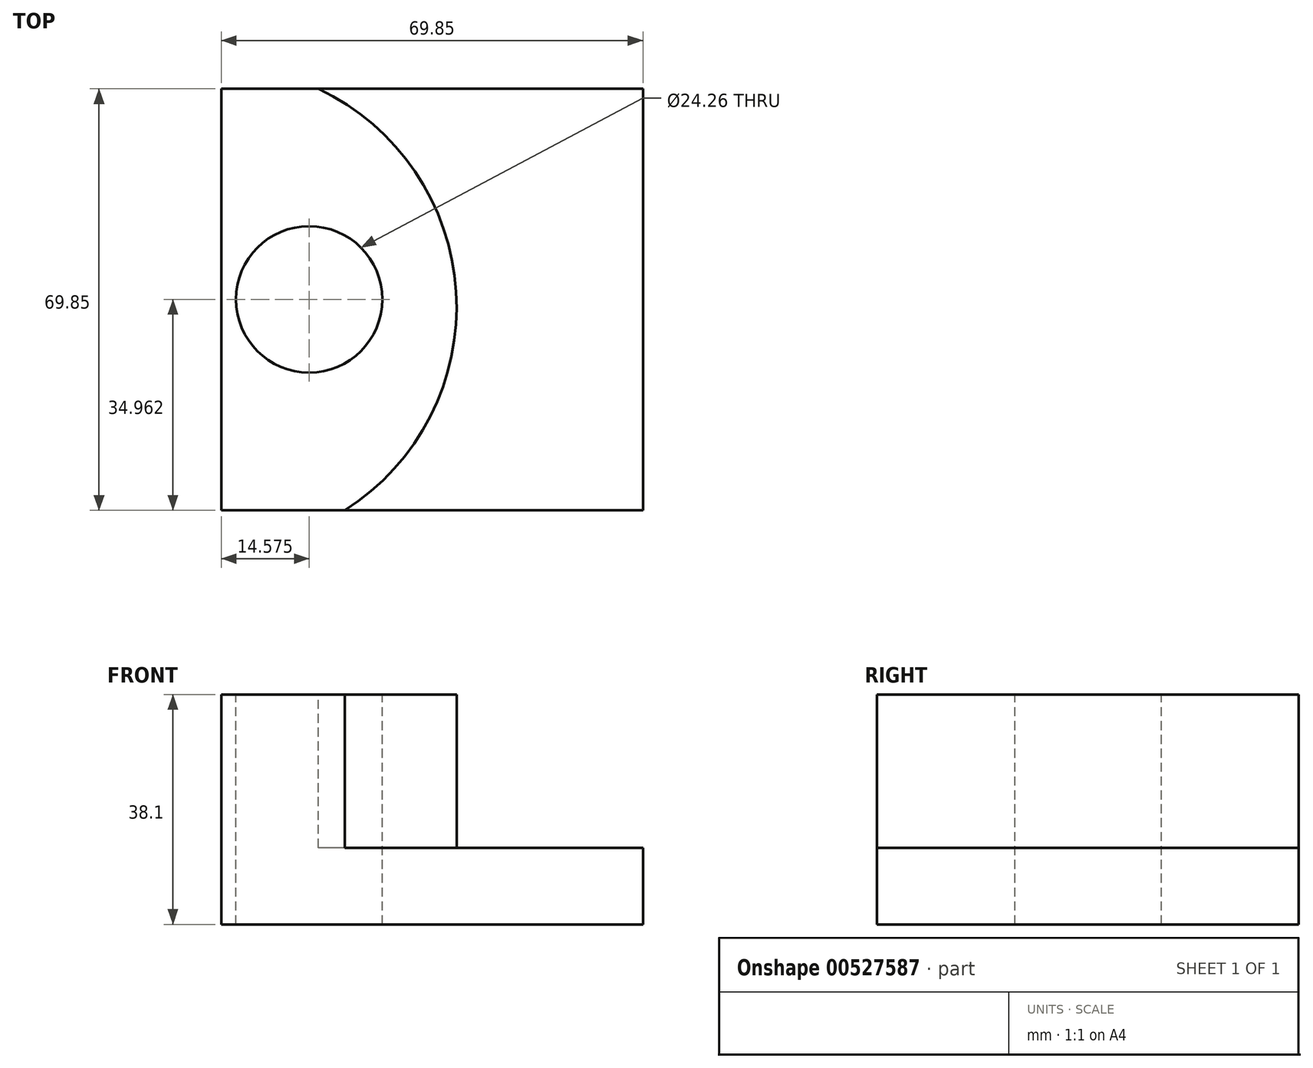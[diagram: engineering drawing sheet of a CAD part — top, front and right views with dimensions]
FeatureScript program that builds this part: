
annotation { "Feature Type Name" : "Feature", "Feature Type Description" : "" }
export const myFeature = defineFeature(function(context is Context, id is Id, definition is map)
    precondition{}
    {
        {
            var Q0;
            Q0=qCreatedBy(makeId("Front.planeOp"),FACE);
            var sketch = newSketch(context, id + "F0", { "sketchPlane" : qUnion([Q0])});
            skLineSegment(sketch, "E0", {"start": v(0, 0) * mm, "end": v(69.85, 0) * mm});
            skLineSegment(sketch, "E1", {"start": v(69.85, 0) * mm, "end": v(69.85, 38.1) * mm});
            skLineSegment(sketch, "E2", {"start": v(69.85, 38.1) * mm, "end": v(0, 38.1) * mm});
            skLineSegment(sketch, "E3", {"start": v(0, 38.1) * mm, "end": v(0, 0) * mm});
            skSolve(sketch);
        }
        {
            var Q0;
            Q0=makeQuery(id+"F0.imprint","IMPRINT",FACE,{"disambiguationData":[TD([[makeQuery(id+"F0.imprint","IMPRINT",EDGE,{"derivedFrom":sQuery(id+"F0.wireOp",EDGE,"E0")}),1.0]])]});
            extrude(context, id + "F1", {"entities" : qUnion([Q0]), "depth" : 69.85 * mm, "offsetDistance" : 25.4 * mm});
        }
        {
            var Q0;
            Q0=makeQuery(id+"F1.opExtrude","SWEPT_FACE",FACE,{"disambiguationData":[OSD([sQuery(id+"F0.wireOp",EDGE,"E2")])]});
            var sketch = newSketch(context, id + "F2", { "sketchPlane" : qUnion([Q0])});
            skArc(sketch, "E4", {"start": v(20.47, -69.85) * mm, "mid": v(38.92, -33.64) * mm, "end": v(16.13, 0) * mm});
            skSolve(sketch);
        }
        {
            var Q0;
            {var subQ0=sQuery(id+"F2.wireOp",EDGE,"E4");Q0=makeQuery(id+"F2.imprint","IMPRINT",FACE,{"disambiguationData":[TD([[makeQuery(id+"F2.imprint","IMPRINT",EDGE,{"derivedFrom":subQ0}),-1.0]])]});}
            extrude(context, id + "F3", {"entities" : qUnion([Q0]), "operationType" : NewBodyOperationType.REMOVE, "oppositeDirection" : true, "depth" : 25.4 * mm, "offsetDistance" : 25.4 * mm});
        }
        {
            var Q0;
            Q0=makeQuery(id+"F1.opExtrude","SWEPT_FACE",FACE,{"disambiguationData":[OSD([sQuery(id+"F0.wireOp",EDGE,"E2")])]});
            var sketch = newSketch(context, id + "F4", { "sketchPlane" : qUnion([Q0])});
            skCircle(sketch, "E5", {"center": v(14.58, -34.89) * mm, "radius": 12.13 * mm});
            skSolve(sketch);
        }
        {
            var Q0;
            Q0=makeQuery(id+"F4.imprint","IMPRINT",FACE,{"disambiguationData":[TD([[makeQuery(id+"F4.imprint","IMPRINT",EDGE,{"derivedFrom":sQuery(id+"F4.wireOp",EDGE,"E5")}),1.0]])]});
            extrude(context, id + "F5", {"entities" : qUnion([Q0]), "operationType" : NewBodyOperationType.REMOVE, "oppositeDirection" : true, "depth" : 38.1 * mm, "offsetDistance" : 25.4 * mm});
        }
    });
